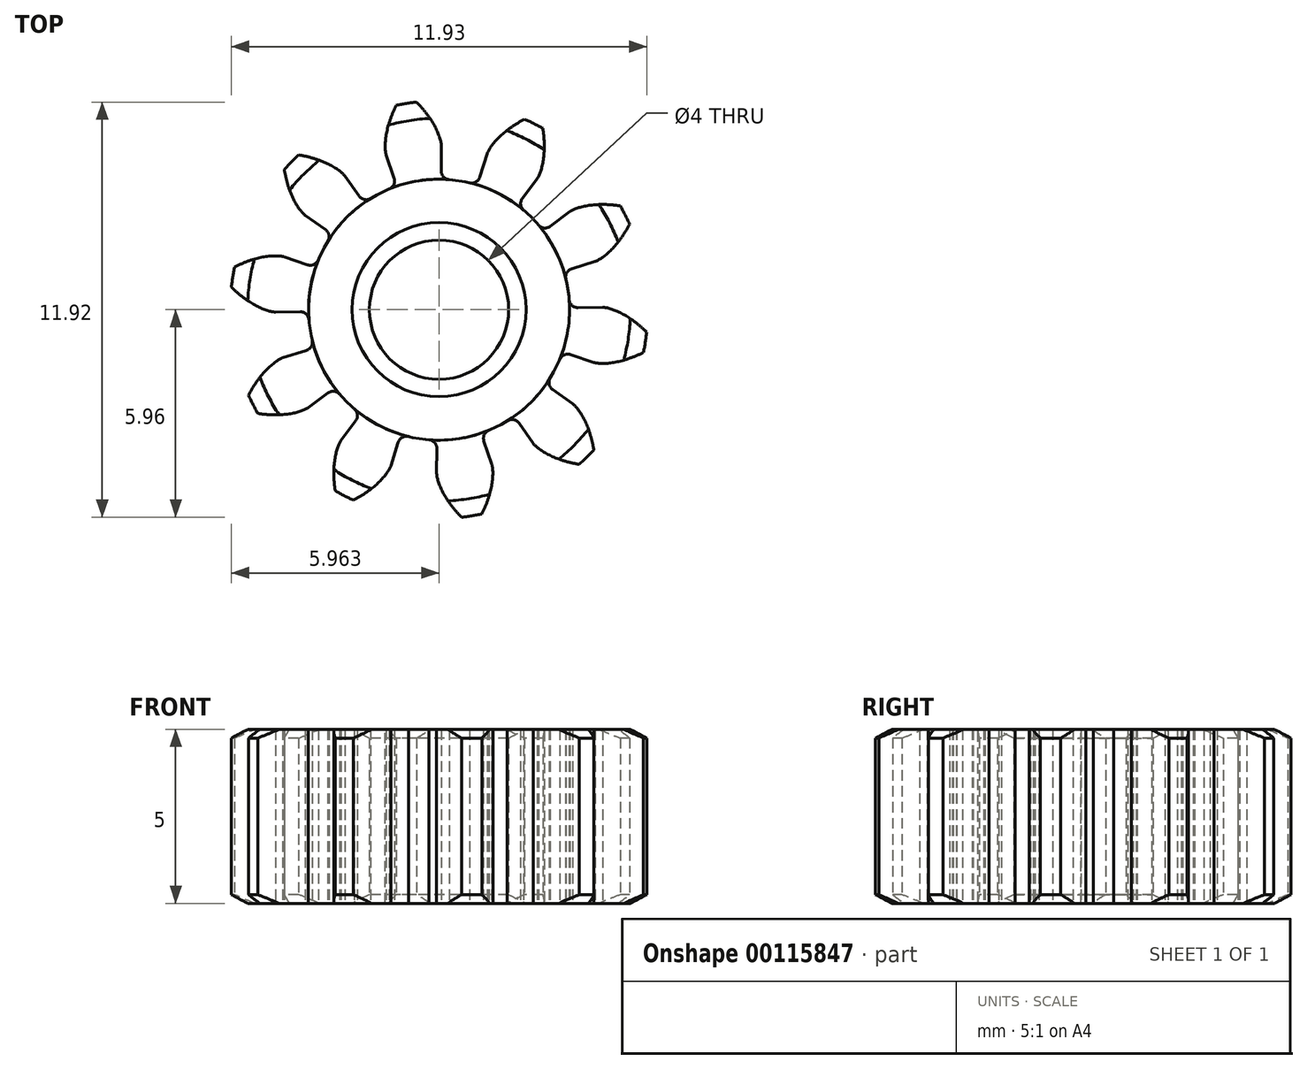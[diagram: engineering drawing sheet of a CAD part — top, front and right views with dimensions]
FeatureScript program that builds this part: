
annotation { "Feature Type Name" : "Feature", "Feature Type Description" : "" }
export const myFeature = defineFeature(function(context is Context, id is Id, definition is map)
    precondition{}
    {
        {
            var Q0;
            Q0=qCreatedBy(makeId("Top.planeOp"),FACE);
            var sketch = newSketch(context, id + "F0", { "sketchPlane" : qUnion([Q0])});
            skArc(sketch, "E0", {"start": v(4.77, -1.23) * mm, "mid": v(4.82, -0.94) * mm, "end": v(4.86, -0.65) * mm});
            skFitSpline(sketch, "E1", {"points": [v(3.6, 0.07) * mm, v(3.6, 0.07) * mm, v(3.6, 0.07) * mm, v(3.6, 0.07) * mm, v(3.6, 0.07) * mm, v(3.6, 0.07) * mm, v(3.6, 0.07) * mm, v(3.62, 0.07) * mm, v(3.63, 0.07) * mm, v(3.64, 0.07) * mm, v(3.65, 0.06) * mm, v(3.66, 0.06) * mm, v(3.68, 0.06) * mm, v(3.7, 0.06) * mm, v(3.71, 0.05) * mm, v(3.73, 0.05) * mm, v(3.75, 0.04) * mm, v(3.77, 0.04) * mm, v(3.8, 0.03) * mm, v(3.82, 0.03) * mm, v(3.84, 0.02) * mm, v(3.87, 0) * mm, v(3.9, 0) * mm, v(3.93, -0.01) * mm, v(3.96, -0.02) * mm, v(3.99, -0.04) * mm, v(4.02, -0.05) * mm, v(4.05, -0.07) * mm, v(4.09, -0.08) * mm, v(4.12, -0.1) * mm, v(4.16, -0.12) * mm, v(4.2, -0.14) * mm, v(4.23, -0.16) * mm, v(4.27, -0.18) * mm, v(4.31, -0.2) * mm, v(4.35, -0.23) * mm, v(4.4, -0.26) * mm, v(4.43, -0.3) * mm, v(4.48, -0.32) * mm, v(4.52, -0.35) * mm, v(4.56, -0.39) * mm, v(4.6, -0.42) * mm, v(4.65, -0.46) * mm, v(4.7, -0.5) * mm, v(4.74, -0.54) * mm, v(4.79, -0.58) * mm, v(4.83, -0.62) * mm, v(4.85, -0.64) * mm, v(4.86, -0.65) * mm]});
            skFitSpline(sketch, "E2", {"points": [v(3.34, -1.52) * mm, v(3.34, -1.52) * mm, v(3.34, -1.52) * mm, v(3.34, -1.52) * mm, v(3.35, -1.52) * mm, v(3.35, -1.52) * mm, v(3.36, -1.52) * mm, v(3.36, -1.53) * mm, v(3.37, -1.53) * mm, v(3.38, -1.53) * mm, v(3.4, -1.53) * mm, v(3.4, -1.53) * mm, v(3.42, -1.54) * mm, v(3.44, -1.54) * mm, v(3.46, -1.54) * mm, v(3.48, -1.54) * mm, v(3.5, -1.54) * mm, v(3.52, -1.54) * mm, v(3.54, -1.55) * mm, v(3.57, -1.55) * mm, v(3.6, -1.55) * mm, v(3.62, -1.55) * mm, v(3.65, -1.54) * mm, v(3.68, -1.54) * mm, v(3.72, -1.54) * mm, v(3.75, -1.54) * mm, v(3.78, -1.54) * mm, v(3.82, -1.53) * mm, v(3.86, -1.53) * mm, v(3.9, -1.52) * mm, v(3.94, -1.51) * mm, v(3.98, -1.5) * mm, v(4.02, -1.5) * mm, v(4.07, -1.49) * mm, v(4.11, -1.48) * mm, v(4.16, -1.46) * mm, v(4.2, -1.45) * mm, v(4.25, -1.44) * mm, v(4.3, -1.42) * mm, v(4.35, -1.4) * mm, v(4.4, -1.38) * mm, v(4.46, -1.36) * mm, v(4.51, -1.34) * mm, v(4.57, -1.32) * mm, v(4.62, -1.3) * mm, v(4.68, -1.27) * mm, v(4.73, -1.25) * mm, v(4.76, -1.23) * mm, v(4.77, -1.23) * mm]});
            skLineSegment(sketch, "E3", {"start": v(3.6, 0.07) * mm, "end": v(2.88, 0.06) * mm});
            skLineSegment(sketch, "E4", {"start": v(2.67, -1.3) * mm, "end": v(3.34, -1.52) * mm});
            skArc(sketch, "E5", {"start": v(2.36, -1.43) * mm, "mid": v(-4.81, 0.59) * mm, "end": v(2.63, 0.3) * mm});
            skPoint(sketch, "E6.visualSharp", {"position": v(2.64, 0.06) * mm});
            skArc(sketch, "E6.filletArc", {"start": v(2.63, 0.3) * mm, "mid": v(2.71, 0.12) * mm, "end": v(2.88, 0.06) * mm});
            skPoint(sketch, "E7.visualSharp", {"position": v(2.44, -1.21) * mm});
            skArc(sketch, "E7.filletArc", {"start": v(2.67, -1.3) * mm, "mid": v(2.49, -1.3) * mm, "end": v(2.36, -1.43) * mm});
            skCircle(sketch, "E8", {"center": v(-1.1, 0) * mm, "radius": 2 * mm});
            skCircle(sketch, "E9", {"center": v(-1.1, 0) * mm, "radius": 3.75 * mm});
            skText(sketch, "E10", { "text": "PCD=10mm", "fontName": "OpenSans-Regular.ttf"});
            const initialGuessF0  = {"E10": [0.00205, -0.00484, 1, 0, 0.0009]};
            skSetInitialGuess(sketch, initialGuessF0);
            skSolve(sketch);
        }
        {
            var Q0;
            Q0=makeQuery(id+"F0.imprint","IMPRINT",FACE,{"disambiguationData":[TD([[makeQuery(id+"F0.imprint","IMPRINT",EDGE,{"derivedFrom":sQuery(id+"F0.wireOp",EDGE,"E0")}),1.0]])]});
            extrude(context, id + "F1", {"entities" : qUnion([Q0]), "depth" : 5 * mm});
        }
        {
            var Q0;
            Q0=makeQuery(id+"F1.opExtrude","CAP_EDGE",EDGE,{"disambiguationData":[OSD([sQuery(id+"F0.wireOp",EDGE,"E0")])],"isStart":false});
            var Q1;
            Q1=makeQuery(id+"F1.opExtrude","CAP_EDGE",EDGE,{"disambiguationData":[OSD([sQuery(id+"F0.wireOp",EDGE,"E0")])],"isStart":true});
            chamfer(context, id + "F2", {"entities" : qUnion([Q0, Q1]), "chamferType" : ChamferType.TWO_OFFSETS, "width1" : .5 * mm, "oppositeDirection" : false, "width2" : .25 * mm, "tangentPropagation" : true});
        }
        {
            var Q0;
            Q0=makeQuery(id+"F1.opExtrude","SWEPT_BODY",BODY,{"disambiguationData":[OSD([sQuery(id+"F0.wireOp",EDGE,"E0"),sQuery(id+"F0.wireOp",EDGE,"E1"),sQuery(id+"F0.wireOp",EDGE,"E2"),sQuery(id+"F0.wireOp",EDGE,"E3"),sQuery(id+"F0.wireOp",EDGE,"E4"),sQuery(id+"F0.wireOp",EDGE,"E6.filletArc"),sQuery(id+"F0.wireOp",EDGE,"E7.filletArc"),sQuery(id+"F0.wireOp",EDGE,"E9")])]});
            var Q1;
            Q1=sQuery(id+"F0.wireOp",EDGE,"E8");
            circularPattern(context, id + "F3", {"entities" : qUnion([Q0]), "axis" : qUnion([Q1]), "angle" : 36 * degree, "instanceCount" : 10});
        }
        {
            var Q0;
            Q0=makeQuery(id+"F0.imprint","IMPRINT",FACE,{"disambiguationData":[TD([[makeQuery(id+"F0.imprint","IMPRINT",EDGE,{"derivedFrom":sQuery(id+"F0.wireOp",EDGE,"E8")}),-1.0]])]});
            extrude(context, id + "F4", {"entities" : qUnion([Q0]), "depth" : 5 * mm});
        }
        {
            var Q0;
            Q0=makeQuery(id+"F4.opExtrude","CAP_EDGE",EDGE,{"disambiguationData":[OSD([sQuery(id+"F0.wireOp",EDGE,"E8")])],"isStart":false});
            var Q1;
            Q1=makeQuery(id+"F4.opExtrude","CAP_EDGE",EDGE,{"disambiguationData":[OSD([sQuery(id+"F0.wireOp",EDGE,"E8")])],"isStart":true});
            chamfer(context, id + "F5", {"entities" : qUnion([Q0, Q1]), "chamferType" : ChamferType.TWO_OFFSETS, "width1" : .25 * mm, "oppositeDirection" : false, "width2" : .5 * mm, "tangentPropagation" : true});
        }
    });
